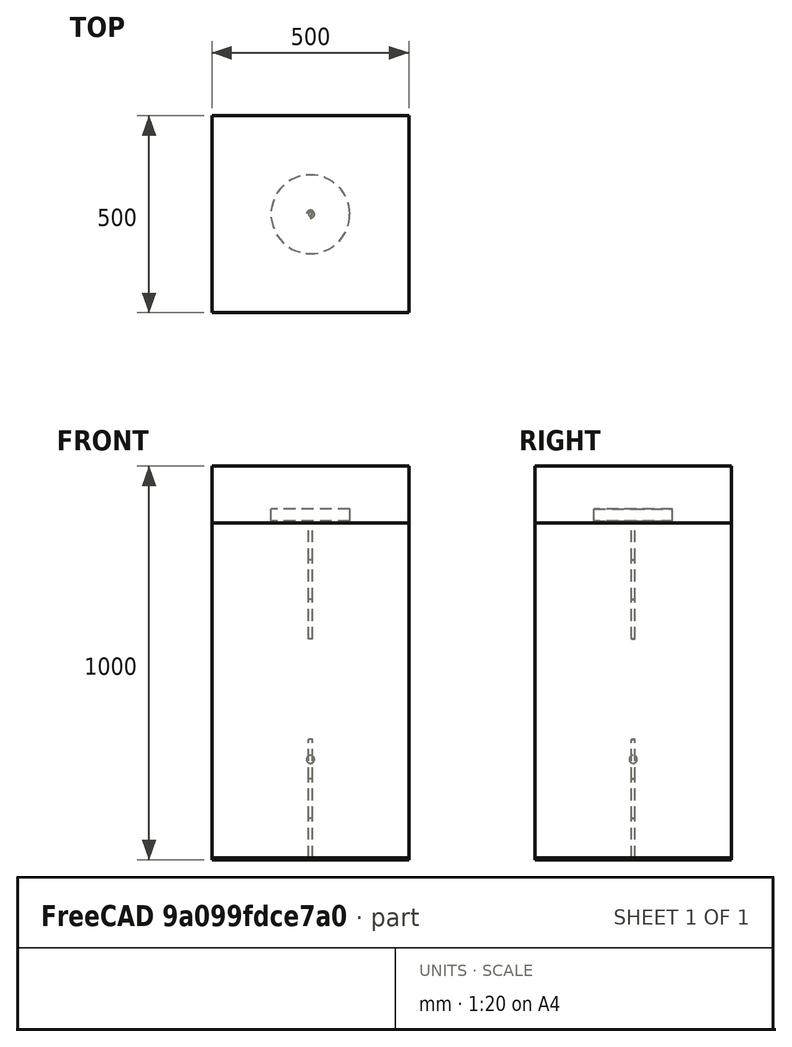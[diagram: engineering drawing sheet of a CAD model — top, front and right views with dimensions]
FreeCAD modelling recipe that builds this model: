
FCSTD DOCUMENT  (FreeCAD 0.18.1R)
Label: DSPH_Case
License: All rights reserved
LicenseURL: http://en.wikipedia.org/wiki/All_rights_reserved
objects: Part::Cylinder×7, Part::Box×3, Mesh::Feature×1, Part::Sphere×1, App::DocumentObjectGroup×1
note: 11 computed .brp shape members not serialized (recipe doc carries the construction recipe); baked Part::Feature solids carry a one-line shape summary decoded from their .brp

FEATURE [Part::Box] Case_Limits  label="Case Limits (3D)"
  AttacherType = Attacher::AttachEngine3D
  Height = 1000
  Length = 500
  Placement = pos=(-250,-250,-5) rot=(0,0,1;0rad)
  Width = 500
FEATURE [Part::Box] Box005  label="Water"
  AttacherType = Attacher::AttachEngine3D
  Height = 850
  Length = 500
  Placement = pos=(-250,-250,0) rot=(0,0,1;0rad)
  Width = 500
FEATURE [Mesh::Feature] ARC2
  Placement = pos=(-155.23,209.5,263.5) rot=(0,0,1;0rad)
FEATURE [Part::Cylinder] Cylinder  label="BRope1"
  Angle = 360
  AttacherType = Attacher::AttachEngine3D
  Height = 100
  Radius = 5
FEATURE [Part::Cylinder] Cylinder001  label="BRope2"
  Angle = 360
  AttacherType = Attacher::AttachEngine3D
  Height = 100
  Placement = pos=(0,0,100) rot=(0,0,1;0rad)
  Radius = 5
FEATURE [Part::Cylinder] Cylinder002  label="BRope3"
  Angle = 360
  AttacherType = Attacher::AttachEngine3D
  Height = 100
  Placement = pos=(0,0,200) rot=(0,0,1;0rad)
  Radius = 5
FEATURE [Part::Cylinder] Cylinder003  label="BRope004"
  Angle = 360
  AttacherType = Attacher::AttachEngine3D
  Height = 100
  Placement = pos=(0,0,556) rot=(0,0,1;0rad)
  Radius = 5
FEATURE [Part::Cylinder] Cylinder004  label="BRope005"
  Angle = 360
  AttacherType = Attacher::AttachEngine3D
  Height = 100
  Placement = pos=(0,0,656) rot=(0,0,1;0rad)
  Radius = 5
FEATURE [Part::Cylinder] Cylinder005  label="BRope006"
  Angle = 360
  AttacherType = Attacher::AttachEngine3D
  Height = 100
  Placement = pos=(0,0,756) rot=(0,0,1;0rad)
  Radius = 5
FEATURE [Part::Cylinder] Cylinder006  label="Cylinder"
  Angle = 360
  AttacherType = Attacher::AttachEngine3D
  Height = 30
  Placement = pos=(0,0,856) rot=(0,0,1;0rad)
  Radius = 100
FEATURE [Part::Sphere] FillPoint
  Angle1 = -90
  Angle2 = 90
  Angle3 = 360
  AttacherType = Attacher::AttachEngine3D
  Placement = pos=(0,0,250) rot=(0,0,1;0rad)
  Radius = 10
FEATURE [Part::Box] FillLimit
  AttacherType = Attacher::AttachEngine3D
  Height = 1
  Length = 1
  Width = 1
FEATURE [App::DocumentObjectGroup] FillBox
  Group = -> [FillLimit,FillPoint]
